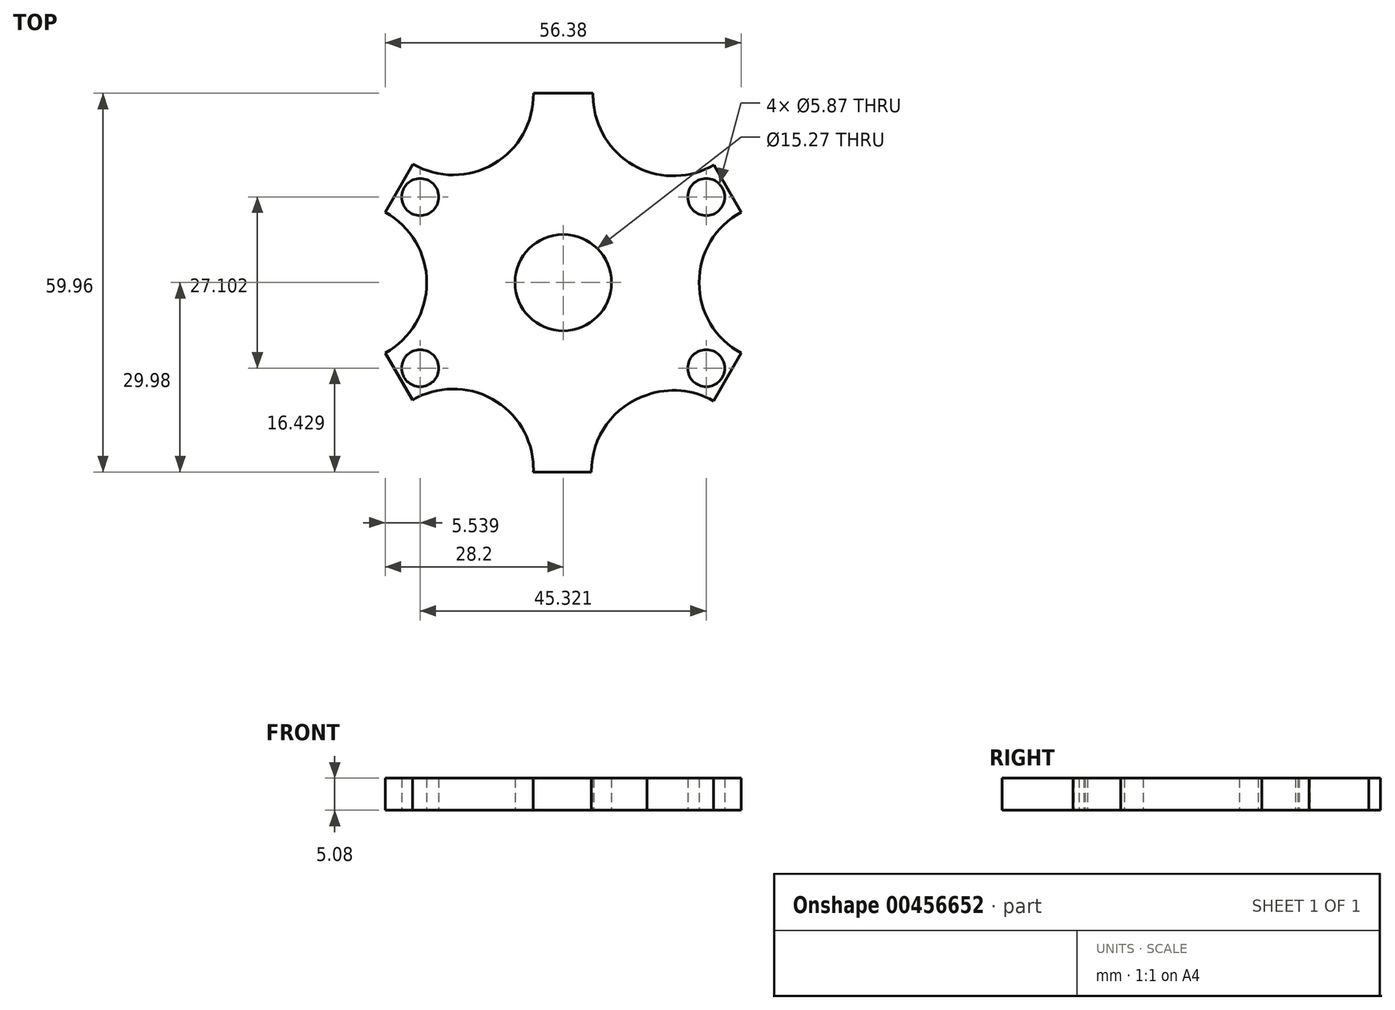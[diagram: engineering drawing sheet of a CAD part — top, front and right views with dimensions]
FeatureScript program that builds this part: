
annotation { "Feature Type Name" : "Feature", "Feature Type Description" : "" }
export const myFeature = defineFeature(function(context is Context, id is Id, definition is map)
    precondition{}
    {
        {
            var Q0;
            Q0=qCreatedBy(makeId("Top.planeOp"),FACE);
            var sketch = newSketch(context, id + "F0", { "sketchPlane" : qUnion([Q0])});
            skCircle(sketch, "E0.cCircle", {"center": v(0, 0) * mm, "radius": 29.98 * mm, "construction": true});
            skLineSegment(sketch, "E0.0", {"start": v(17.31, -29.98) * mm, "end": v(-17.31, -29.98) * mm});
            skLineSegment(sketch, "E0.1", {"start": v(-17.31, -29.98) * mm, "end": v(-34.62, 0) * mm});
            skLineSegment(sketch, "E0.2", {"start": v(-34.62, 0) * mm, "end": v(-17.31, 29.98) * mm});
            skLineSegment(sketch, "E0.3", {"start": v(-17.31, 29.98) * mm, "end": v(17.31, 29.98) * mm});
            skLineSegment(sketch, "E0.4", {"start": v(17.31, 29.98) * mm, "end": v(34.62, 0) * mm});
            skLineSegment(sketch, "E0.5", {"start": v(34.62, 0) * mm, "end": v(17.31, -29.98) * mm});
            skPoint(sketch, "E0.0.midPoint", {"position": v(0, -29.98) * mm});
            skSolve(sketch);
        }
        {
            var Q0;
            Q0 = qSketchRegion(id + "F0", true);
            extrude(context, id + "F1", {"entities" : qUnion([Q0]), "depth" : 5.08 * mm});
        }
        {
            var Q0;
            Q0=qCreatedBy(makeId("Top.planeOp"),FACE);
            var sketch = newSketch(context, id + "F2", { "sketchPlane" : qUnion([Q0])});
            skCircle(sketch, "E1", {"center": v(0, 0) * mm, "radius": 7.63 * mm});
            skSolve(sketch);
        }
        {
            var Q0;
            Q0=sQuery(id+"F2.wireOp",VERTEX,"E1.center");
            var Q1;
            Q1=makeQuery(id+"F1.opExtrude","SWEPT_BODY",BODY,{"disambiguationData":[OSD([sQuery(id+"F0.wireOp",EDGE,"E0.0"),sQuery(id+"F0.wireOp",EDGE,"E0.1"),sQuery(id+"F0.wireOp",EDGE,"E0.2"),sQuery(id+"F0.wireOp",EDGE,"E0.3"),sQuery(id+"F0.wireOp",EDGE,"E0.4"),sQuery(id+"F0.wireOp",EDGE,"E0.5")])]});
            hole(context, id + "F3", {"style" : HoleStyle.SIMPLE, "endStyle" : HoleEndStyle.THROUGH, "oppositeDirection" : true, "holeDiameter" : 15.27 * mm, "isTappedThrough" : true, "tappedDepth" : 12.7 * mm, "tapClearance" : 3, "locations" : qUnion([Q0]), "scope" : qUnion([Q1])});
        }
        {
            var Q0;
            Q0=qCreatedBy(makeId("Top.planeOp"),FACE);
            var sketch = newSketch(context, id + "F4", { "sketchPlane" : qUnion([Q0])});
            skLineSegment(sketch, "E2", {"start": v(7.63, 0) * mm, "end": v(34.24, 0) * mm});
            skLineSegment(sketch, "E3", {"start": v(7.63, 0) * mm, "end": v(17.17, -29.88) * mm});
            skLineSegment(sketch, "E4", {"start": v(7.63, 0) * mm, "end": v(17.42, 29.75) * mm});
            skLineSegment(sketch, "E5", {"start": v(-7.7, 0) * mm, "end": v(-34.48, 0) * mm});
            skPoint(sketch, "E5.startSnap0", {"position": v(20.93, 0) * mm});
            skLineSegment(sketch, "E6", {"start": v(-7.7, 0) * mm, "end": v(-17.42, -29.53) * mm});
            skLineSegment(sketch, "E7", {"start": v(-17.42, -29.53) * mm, "end": v(-7.7, 0) * mm});
            skLineSegment(sketch, "E8", {"start": v(-7.7, 0) * mm, "end": v(-17.42, 29.75) * mm});
            skSolve(sketch);
        }
        {
            var Q0;
            Q0=qCreatedBy(makeId("Top.planeOp"),FACE);
            var sketch = newSketch(context, id + "F5", { "sketchPlane" : qUnion([Q0])});
            skArc(sketch, "E9", {"start": v(17.44, 29.6) * mm, "mid": v(18.98, 10.9) * mm, "end": v(34.24, 0) * mm});
            skArc(sketch, "E10", {"start": v(34.24, 0) * mm, "mid": v(18.28, -10.62) * mm, "end": v(17.5, -29.76) * mm});
            skArc(sketch, "E11", {"start": v(-17.42, -29.56) * mm, "mid": v(-19.3, -11.03) * mm, "end": v(-34.32, 0) * mm});
            skArc(sketch, "E12", {"start": v(-34.32, 0) * mm, "mid": v(-18.6, 10.82) * mm, "end": v(-17.6, 29.88) * mm});
            skSolve(sketch);
        }
        {
            var Q0;
            Q0=sQuery(id+"F5.wireOp",VERTEX,"E11.start");
            var Q1;
            Q1=sQuery(id+"F5.wireOp",VERTEX,"E12.start");
            var Q2;
            Q2=sQuery(id+"F5.wireOp",VERTEX,"E12.end");
            var Q3;
            Q3=sQuery(id+"F5.wireOp",VERTEX,"E9.start");
            var Q4;
            Q4=sQuery(id+"F5.wireOp",VERTEX,"E9.end");
            var Q5;
            Q5=sQuery(id+"F4.wireOp",VERTEX,"E7.start");
            var Q6;
            Q6=sQuery(id+"F4.wireOp",VERTEX,"E8.end");
            var Q7;
            Q7=sQuery(id+"F4.wireOp",VERTEX,"E4.end");
            var Q8;
            Q8=sQuery(id+"F4.wireOp",VERTEX,"E2.end");
            var Q9;
            Q9=sQuery(id+"F4.wireOp",VERTEX,"E3.end");
            var Q10;
            Q10=sQuery(id+"F5.wireOp",VERTEX,"E10.end");
            var Q11;
            Q11=makeQuery(id+"F1.opExtrude","SWEPT_BODY",BODY,{"disambiguationData":[OSD([sQuery(id+"F0.wireOp",EDGE,"E0.0"),sQuery(id+"F0.wireOp",EDGE,"E0.1"),sQuery(id+"F0.wireOp",EDGE,"E0.2"),sQuery(id+"F0.wireOp",EDGE,"E0.3"),sQuery(id+"F0.wireOp",EDGE,"E0.4"),sQuery(id+"F0.wireOp",EDGE,"E0.5")])]});
            hole(context, id + "F6", {"style" : HoleStyle.SIMPLE, "endStyle" : HoleEndStyle.THROUGH, "oppositeDirection" : true, "holeDiameter" : 25.4 * mm, "isTappedThrough" : true, "tappedDepth" : 12.7 * mm, "tapClearance" : 3, "locations" : qUnion([Q0, Q1, Q2, Q3, Q4, Q5, Q6, Q7, Q8, Q9, Q10]), "scope" : qUnion([Q11])});
        }
        {
            var Q0;
            Q0=qCreatedBy(makeId("Top.planeOp"),FACE);
            var sketch = newSketch(context, id + "F7", { "sketchPlane" : qUnion([Q0])});
            skCircle(sketch, "E13", {"center": v(-22.66, 13.55) * mm, "radius": 3.04 * mm});
            skCircle(sketch, "E14.MirrorC", {"center": v(22.66, 13.55) * mm, "radius": 3.04 * mm});
            skCircle(sketch, "E15.MirrorC", {"center": v(-22.66, -13.55) * mm, "radius": 3.04 * mm});
            skCircle(sketch, "E16.MirrorC", {"center": v(22.66, -13.55) * mm, "radius": 3.04 * mm});
            skSolve(sketch);
        }
        {
            var Q0;
            Q0=sQuery(id+"F7.wireOp",VERTEX,"E13.center");
            var Q1;
            Q1=sQuery(id+"F7.wireOp",VERTEX,"E15.MirrorC.center");
            var Q2;
            Q2=sQuery(id+"F7.wireOp",VERTEX,"E14.MirrorC.center");
            var Q3;
            Q3=sQuery(id+"F7.wireOp",VERTEX,"E16.MirrorC.center");
            var Q4;
            Q4=makeQuery(id+"F1.opExtrude","SWEPT_BODY",BODY,{"disambiguationData":[OSD([sQuery(id+"F0.wireOp",EDGE,"E0.0"),sQuery(id+"F0.wireOp",EDGE,"E0.1"),sQuery(id+"F0.wireOp",EDGE,"E0.2"),sQuery(id+"F0.wireOp",EDGE,"E0.3"),sQuery(id+"F0.wireOp",EDGE,"E0.4"),sQuery(id+"F0.wireOp",EDGE,"E0.5")])]});
            hole(context, id + "F8", {"style" : HoleStyle.SIMPLE, "endStyle" : HoleEndStyle.THROUGH, "oppositeDirection" : true, "holeDiameter" : 5.87 * mm, "isTappedThrough" : true, "tappedDepth" : 12.7 * mm, "tapClearance" : 3, "locations" : qUnion([Q0, Q1, Q2, Q3]), "scope" : qUnion([Q4])});
        }
    });
